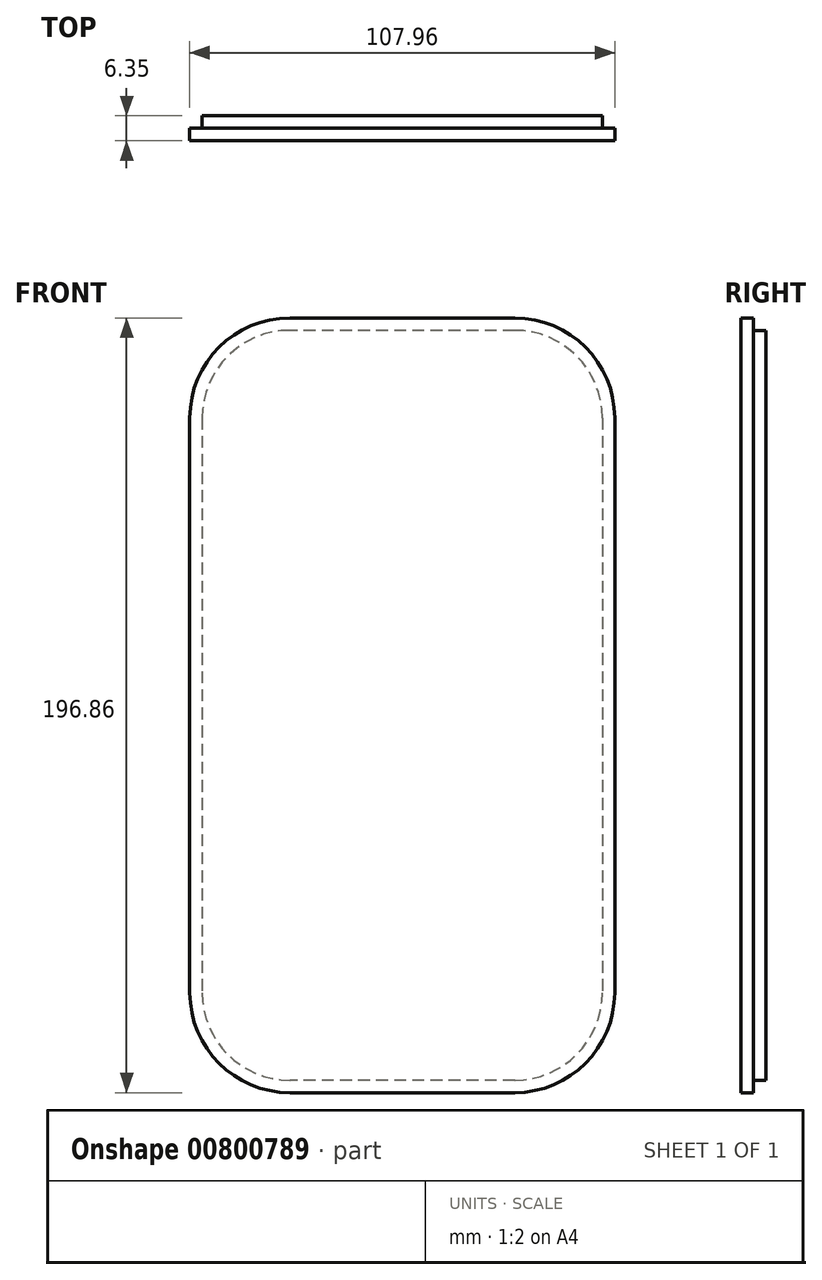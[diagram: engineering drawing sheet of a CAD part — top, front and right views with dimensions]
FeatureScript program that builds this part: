
annotation { "Feature Type Name" : "Feature", "Feature Type Description" : "" }
export const myFeature = defineFeature(function(context is Context, id is Id, definition is map)
    precondition{}
    {
        {
            var Q0;
            Q0=qCreatedBy(makeId("Front.planeOp"),FACE);
            var sketch = newSketch(context, id + "F0", { "sketchPlane" : qUnion([Q0])});
            skArc(sketch, "E0.0", {"start": v(50.8, 73.03) * mm, "mid": v(44.3, 88.74) * mm, "end": v(28.57, 95.25) * mm});
            skLineSegment(sketch, "E0.1", {"start": v(50.8, 73.03) * mm, "end": v(50.8, -73.03) * mm});
            skLineSegment(sketch, "E0.2", {"start": v(28.57, 95.25) * mm, "end": v(-28.58, 95.25) * mm});
            skArc(sketch, "E0.3", {"start": v(28.58, -95.25) * mm, "mid": v(44.3, -88.74) * mm, "end": v(50.8, -73.03) * mm});
            skArc(sketch, "E0.4", {"start": v(-28.58, 95.25) * mm, "mid": v(-44.3, 88.74) * mm, "end": v(-50.8, 73.03) * mm});
            skLineSegment(sketch, "E0.5", {"start": v(-50.8, 73.03) * mm, "end": v(-50.8, -73.03) * mm});
            skArc(sketch, "E0.6", {"start": v(-50.8, -73.03) * mm, "mid": v(-44.3, -88.74) * mm, "end": v(-28.57, -95.25) * mm});
            skLineSegment(sketch, "E0.7", {"start": v(28.58, -95.25) * mm, "end": v(-28.57, -95.25) * mm});
            skSolve(sketch);
        }
        {
            var Q0;
            Q0=makeQuery(id+"F0.imprint","IMPRINT",FACE,{"disambiguationData":[TD([[makeQuery(id+"F0.imprint","IMPRINT",EDGE,{"derivedFrom":sQuery(id+"F0.wireOp",EDGE,"E0.0")}),1.0]])]});
            extrude(context, id + "F1", {"entities" : qUnion([Q0]), "depth" : 3.17 * mm, "offsetDistance" : 25.4 * mm});
        }
        {
            var Q0;
            Q0=makeQuery(id+"F1.opExtrude","CAP_FACE",FACE,{"disambiguationData":[OSD([sQuery(id+"F0.wireOp",EDGE,"E0.0"),sQuery(id+"F0.wireOp",EDGE,"E0.1"),sQuery(id+"F0.wireOp",EDGE,"E0.2"),sQuery(id+"F0.wireOp",EDGE,"E0.3"),sQuery(id+"F0.wireOp",EDGE,"E0.4"),sQuery(id+"F0.wireOp",EDGE,"E0.5"),sQuery(id+"F0.wireOp",EDGE,"E0.6"),sQuery(id+"F0.wireOp",EDGE,"E0.7")])],"isStart":false});
            var sketch = newSketch(context, id + "F2", { "sketchPlane" : qUnion([Q0])});
            skArc(sketch, "E1.0", {"start": v(-53.97, -73.03) * mm, "mid": v(-46.54, -90.99) * mm, "end": v(-28.57, -98.43) * mm});
            skLineSegment(sketch, "E1.1", {"start": v(-53.98, 73.03) * mm, "end": v(-53.97, -73.03) * mm});
            skLineSegment(sketch, "E1.2", {"start": v(-28.57, -98.43) * mm, "end": v(28.58, -98.43) * mm});
            skArc(sketch, "E1.3", {"start": v(-28.58, 98.43) * mm, "mid": v(-46.54, 90.99) * mm, "end": v(-53.98, 73.03) * mm});
            skArc(sketch, "E1.4", {"start": v(28.58, -98.43) * mm, "mid": v(46.54, -90.99) * mm, "end": v(53.98, -73.03) * mm});
            skLineSegment(sketch, "E1.5", {"start": v(53.98, -73.03) * mm, "end": v(53.97, 73.03) * mm});
            skArc(sketch, "E1.6", {"start": v(53.97, 73.03) * mm, "mid": v(46.54, 90.99) * mm, "end": v(28.57, 98.43) * mm});
            skLineSegment(sketch, "E1.7", {"start": v(28.57, 98.43) * mm, "end": v(-28.58, 98.43) * mm});
            skSolve(sketch);
        }
        {
            var Q0;
            Q0 = qSketchRegion(id + "F2", true);
            extrude(context, id + "F3", {"entities" : qUnion([Q0]), "operationType" : NewBodyOperationType.ADD, "depth" : 3.17 * mm, "offsetDistance" : 25.4 * mm});
        }
    });
